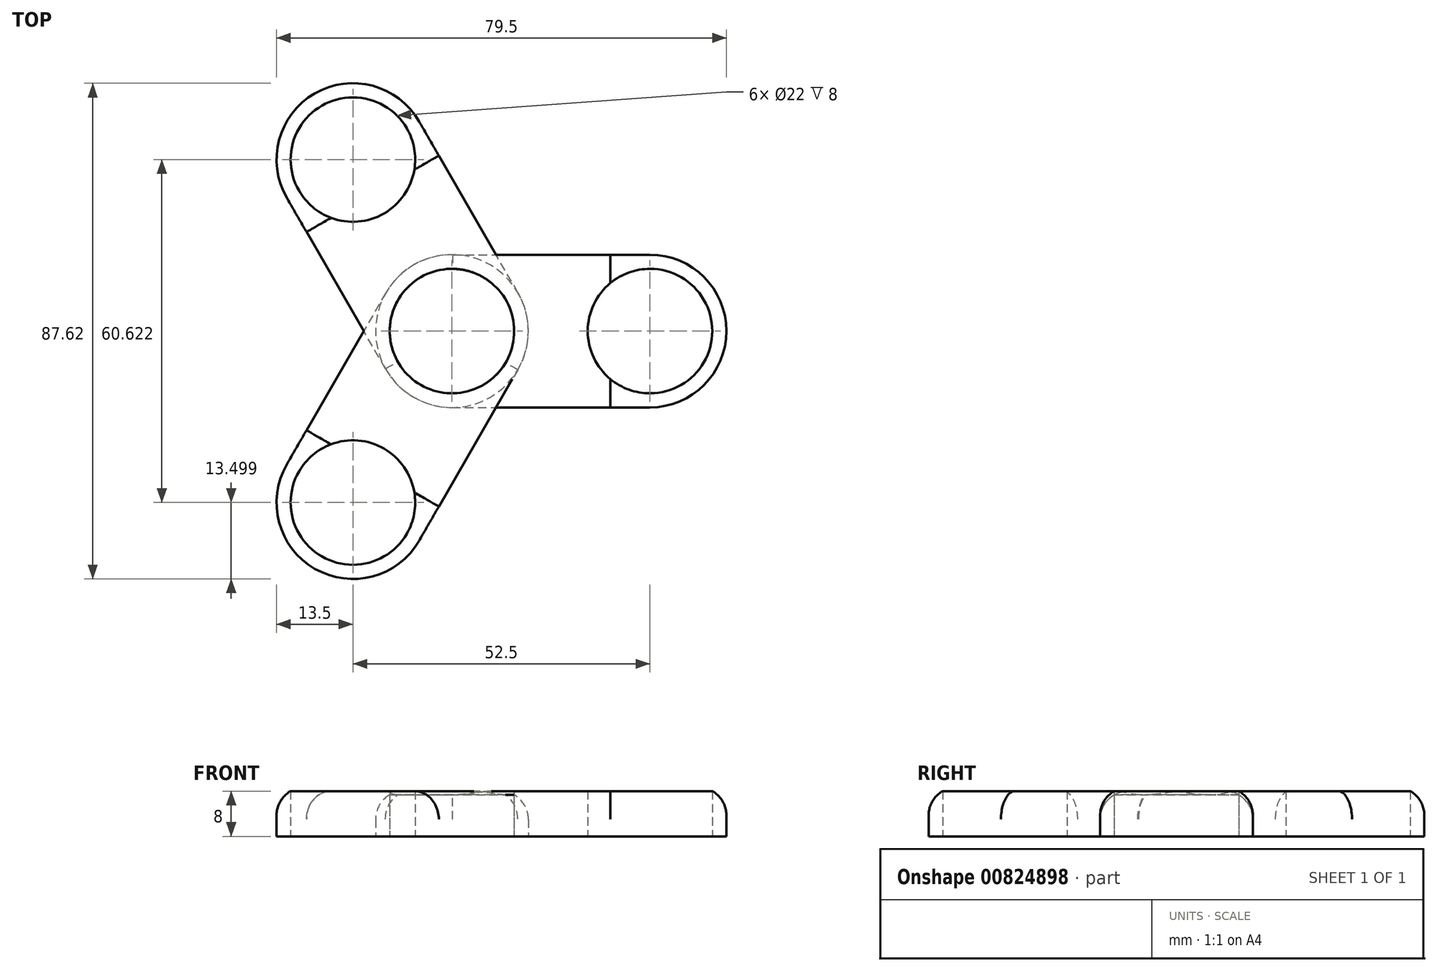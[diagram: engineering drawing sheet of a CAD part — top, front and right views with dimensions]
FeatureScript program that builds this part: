
annotation { "Feature Type Name" : "Feature", "Feature Type Description" : "" }
export const myFeature = defineFeature(function(context is Context, id is Id, definition is map)
    precondition{}
    {
        {
            var Q0;
            Q0=qCreatedBy(makeId("Top.planeOp"),FACE);
            var sketch = newSketch(context, id + "F0", { "sketchPlane" : qUnion([Q0])});
            skCircle(sketch, "E0", {"center": v(0, 0) * mm, "radius": 11 * mm});
            skCircle(sketch, "E1", {"center": v(0, 0) * mm, "radius": 13.5 * mm});
            skLineSegment(sketch, "E2", {"start": v(0, 0) * mm, "end": v(35, 0) * mm, "construction": true});
            skCircle(sketch, "E3", {"center": v(35, 0) * mm, "radius": 11 * mm});
            skCircle(sketch, "E4", {"center": v(35, 0) * mm, "radius": 13.5 * mm});
            skLineSegment(sketch, "E5", {"start": v(0.1, 13.5) * mm, "end": v(35, 13.5) * mm});
            skLineSegment(sketch, "E6", {"start": v(0, -13.5) * mm, "end": v(35, -13.5) * mm});
            skSolve(sketch);
        }
        {
            var Q0;
            Q0=makeQuery(id+"F0.imprint","IMPRINT",FACE,{"disambiguationData":[TD([[makeQuery(id+"F0.imprint","IMPRINT",EDGE,{"derivedFrom":sQuery(id+"F0.wireOp",EDGE,"E0")}),-1.0]])]});
            var Q1;
            {var subQ0=sQuery(id+"F0.wireOp",EDGE,"E5");Q1=makeQuery(id+"F0.imprint","IMPRINT",FACE,{"disambiguationData":[TD([[makeQuery(id+"F0.imprint","IMPRINT",EDGE,{"derivedFrom":subQ0}),-1.0]])]});}
            var Q2;
            Q2=makeQuery(id+"F0.imprint","IMPRINT",FACE,{"disambiguationData":[TD([[makeQuery(id+"F0.imprint","IMPRINT",EDGE,{"derivedFrom":sQuery(id+"F0.wireOp",EDGE,"E3")}),-1.0]])]});
            extrude(context, id + "F1", {"entities" : qUnion([Q0, Q1, Q2]), "depth" : 8 * mm, "offsetDistance" : 25 * mm});
        }
        {
            var Q0;
            Q0=qCreatedBy(makeId("Front.planeOp"),FACE);
            var sketch = newSketch(context, id + "F2", { "sketchPlane" : qUnion([Q0])});
            skLineSegment(sketch, "E7", {"start": v(0, 0) * mm, "end": v(0, 51.67) * mm, "construction": true});
            skSolve(sketch);
        }
        {
            var Q0;
            Q0=makeQuery(id+"F1.opExtrude","SWEPT_BODY",BODY,{"disambiguationData":[OSD([sQuery(id+"F0.wireOp",EDGE,"E0"),sQuery(id+"F0.wireOp",EDGE,"E1"),sQuery(id+"F0.wireOp",EDGE,"E3"),sQuery(id+"F0.wireOp",EDGE,"E4"),sQuery(id+"F0.wireOp",EDGE,"E5"),sQuery(id+"F0.wireOp",EDGE,"E6")])]});
            var Q1;
            Q1=sQuery(id+"F2.wireOp",EDGE,"E7");
            circularPattern(context, id + "F3", {"entities" : qUnion([Q0]), "axis" : qUnion([Q1]), "angle" : 360 * degree, "instanceCount" : 3, "equalSpace" : true});
        }
        {
            var Q0;
            Q0=makeQuery(id+"F3.opPattern","COPY",EDGE,{"derivedFrom":makeQuery(id+"F1.opExtrude","CAP_EDGE",EDGE,{"disambiguationData":[OSD([sQuery(id+"F0.wireOp",EDGE,"E5")])],"isStart":false}),"instanceName":"1"});
            var Q1;
            Q1=makeQuery(id+"F3.opPattern","COPY",EDGE,{"derivedFrom":makeQuery(id+"F1.opExtrude","CAP_EDGE",EDGE,{"disambiguationData":[OSD([sQuery(id+"F0.wireOp",EDGE,"E6")])],"isStart":false}),"instanceName":"2"});
            var Q2;
            Q2=makeQuery(id+"F1.opExtrude","CAP_EDGE",EDGE,{"disambiguationData":[OSD([sQuery(id+"F0.wireOp",EDGE,"E6")])],"isStart":false});
            fillet(context, id + "F4", {"entities" : qUnion([Q0, Q1, Q2]), "radius" : 5 * mm, "tangentPropagation" : true, "allowEdgeOverflow" : false});
        }
    });
